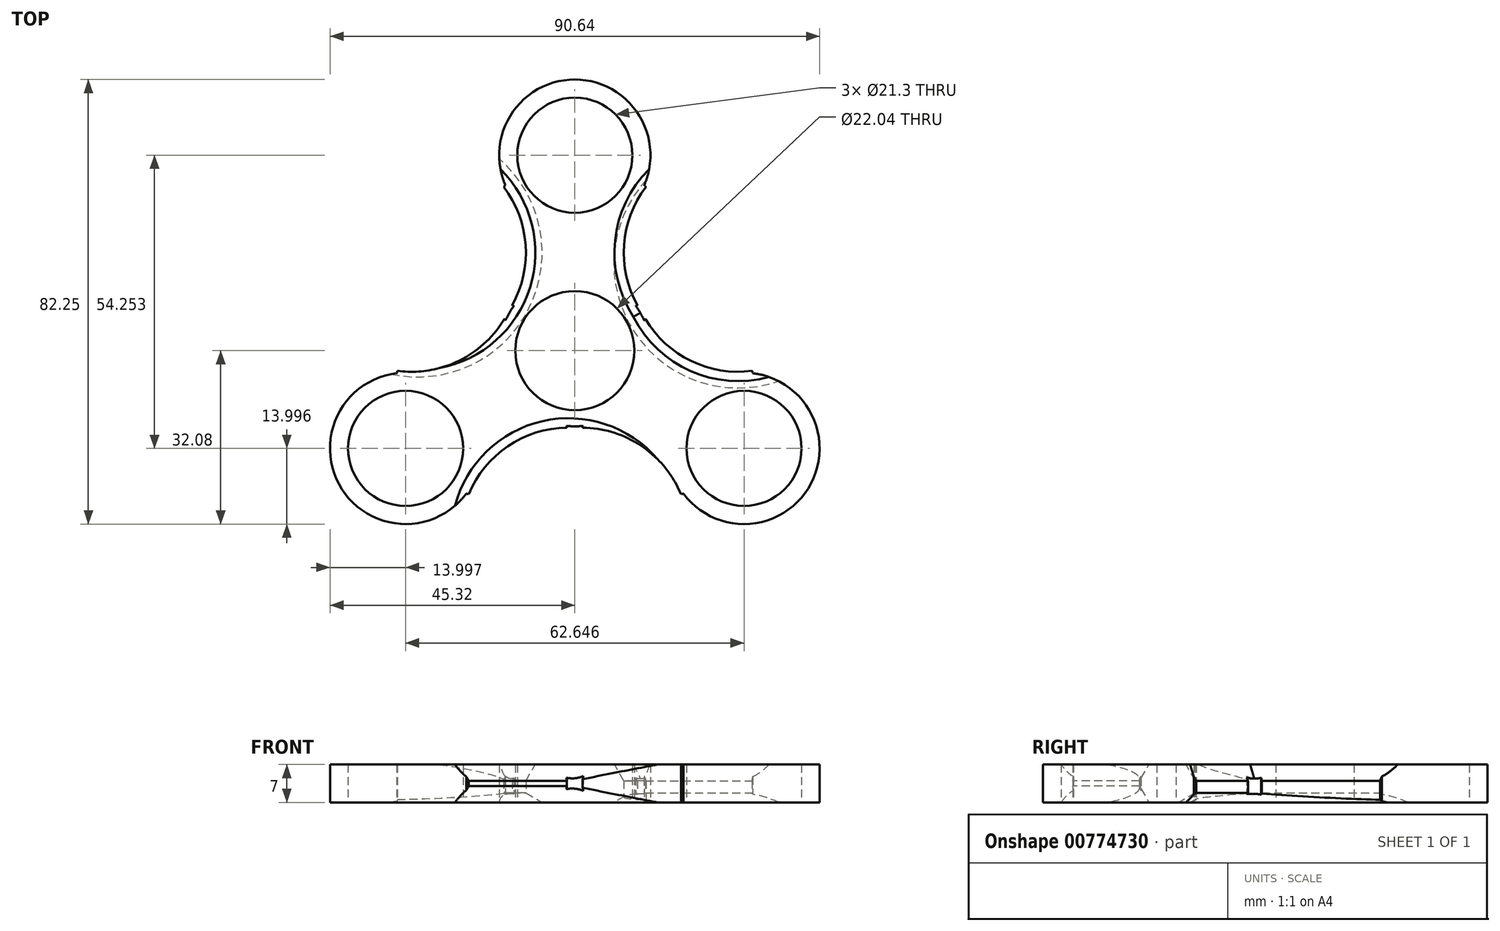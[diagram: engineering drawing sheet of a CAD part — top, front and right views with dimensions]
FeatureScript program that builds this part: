
annotation { "Feature Type Name" : "Feature", "Feature Type Description" : "" }
export const myFeature = defineFeature(function(context is Context, id is Id, definition is map)
    precondition{}
    {
        {
            var Q0;
            Q0=qCreatedBy(makeId("Top.planeOp"),FACE);
            var sketch = newSketch(context, id + "F0", { "sketchPlane" : qUnion([Q0])});
            skCircle(sketch, "E0", {"center": v(0, 0) * mm, "radius": 14 * mm});
            skCircle(sketch, "E1", {"center": v(0, 36.17) * mm, "radius": 14 * mm});
            skPoint(sketch, "E2", {"position": v(0, 18.13) * mm});
            skCircle(sketch, "E3", {"center": v(29.06, 18.13) * mm, "radius": 20 * mm});
            skPoint(sketch, "E4", {"position": v(-29.06, 0) * mm});
            skCircle(sketch, "E5", {"center": v(-29.06, 18.13) * mm, "radius": 20 * mm});
            skCircle(sketch, "E6", {"center": v(0, 18.13) * mm, "radius": 17.93 * mm});
            skCircle(sketch, "E7.1.0", {"center": v(-31.32, -18.08) * mm, "radius": 14 * mm});
            skCircle(sketch, "E7.1.2", {"center": v(-30.23, 16.1) * mm, "radius": 20 * mm});
            skCircle(sketch, "E7.1.3", {"center": v(-1.18, -34.23) * mm, "radius": 20 * mm});
            skCircle(sketch, "E7.1.4", {"center": v(-15.7, -9.07) * mm, "radius": 17.93 * mm});
            skCircle(sketch, "E7.2.0", {"center": v(31.32, -18.08) * mm, "radius": 14 * mm});
            skCircle(sketch, "E7.2.2", {"center": v(1.18, -34.23) * mm, "radius": 20 * mm});
            skCircle(sketch, "E7.2.3", {"center": v(30.23, 16.1) * mm, "radius": 20 * mm});
            skCircle(sketch, "E7.2.4", {"center": v(15.7, -9.07) * mm, "radius": 17.93 * mm});
            skCircle(sketch, "E8", {"center": v(0, 0) * mm, "radius": 11.02 * mm});
            skCircle(sketch, "E9", {"center": v(0, 36.17) * mm, "radius": 10.65 * mm});
            skCircle(sketch, "E10", {"center": v(-31.32, -18.08) * mm, "radius": 10.65 * mm});
            skCircle(sketch, "E11", {"center": v(31.32, -18.08) * mm, "radius": 10.65 * mm});
            skSolve(sketch);
        }
        {
            var Q0;
            {var subQ0=sQuery(id+"F0.wireOp",EDGE,"E7.2.4");var subQ1=sQuery(id+"F0.wireOp",EDGE,"E7.2.0");var subQ2=makeQuery(id+"F0.imprint","INTERSECT",VERTEX,{"disambiguationData":[OD(0.0)],"derivedFrom":[subQ1,subQ0]});Q0=makeQuery(id+"F0.imprint","IMPRINT",FACE,{"disambiguationData":[TD([[makeQuery(id+"F0.imprint","IMPRINT",EDGE,{"disambiguationData":[TD([[subQ2,-1.0]])],"derivedFrom":subQ1}),1.0]])]});}
            var Q1;
            {var subQ0=sQuery(id+"F0.wireOp",EDGE,"E7.2.4");var subQ1=sQuery(id+"F0.wireOp",EDGE,"E7.2.0");var subQ2=makeQuery(id+"F0.imprint","INTERSECT",VERTEX,{"disambiguationData":[OD(0.0)],"derivedFrom":[subQ1,subQ0]});Q1=makeQuery(id+"F0.imprint","IMPRINT",FACE,{"disambiguationData":[TD([[makeQuery(id+"F0.imprint","IMPRINT",EDGE,{"disambiguationData":[TD([[subQ2,1.0]])],"derivedFrom":subQ1}),1.0]])]});}
            var Q2;
            {var subQ5=sQuery(id+"F0.wireOp",EDGE,"E0");var subQ9=sQuery(id+"F0.wireOp",EDGE,"E6");var subQ10=makeQuery(id+"F0.imprint","INTERSECT",VERTEX,{"disambiguationData":[OD(0.0)],"derivedFrom":[subQ5,subQ9]});Q2=makeQuery(id+"F0.imprint","IMPRINT",FACE,{"disambiguationData":[TD([[makeQuery(id+"F0.imprint","IMPRINT",EDGE,{"disambiguationData":[TD([[subQ10,1.0]])],"derivedFrom":subQ5}),-1.0]])]});}
            var Q3;
            {var subQ0=sQuery(id+"F0.wireOp",EDGE,"E6");var subQ1=sQuery(id+"F0.wireOp",EDGE,"B8NFszW9-JFWc-HDjk-8WFd-a5gvqLxuiGRg");var subQ2=makeQuery(id+"F0.imprint","INTERSECT",VERTEX,{"disambiguationData":[OD(0.0)],"derivedFrom":[subQ1,subQ0]});Q3=makeQuery(id+"F0.imprint","IMPRINT",FACE,{"disambiguationData":[TD([[makeQuery(id+"F0.imprint","IMPRINT",EDGE,{"disambiguationData":[TD([[subQ2,1.0]])],"derivedFrom":subQ1}),-1.0]])]});}
            var Q4;
            {var subQ0=sQuery(id+"F0.wireOp",EDGE,"E6");var subQ1=sQuery(id+"F0.wireOp",EDGE,"B8NFszW9-JFWc-HDjk-8WFd-a5gvqLxuiGRg");var subQ2=makeQuery(id+"F0.imprint","INTERSECT",VERTEX,{"disambiguationData":[OD(1.0)],"derivedFrom":[subQ1,subQ0]});Q4=makeQuery(id+"F0.imprint","IMPRINT",FACE,{"disambiguationData":[TD([[makeQuery(id+"F0.imprint","IMPRINT",EDGE,{"disambiguationData":[TD([[subQ2,-1.0]])],"derivedFrom":subQ1}),-1.0]])]});}
            var Q5;
            {var subQ0=sQuery(id+"F0.wireOp",EDGE,"E7.2.4");var subQ1=sQuery(id+"F0.wireOp",EDGE,"B8NFszW9-JFWc-HDjk-8WFd-a5gvqLxuiGRg");var subQ2=makeQuery(id+"F0.imprint","INTERSECT",VERTEX,{"disambiguationData":[OD(1.0)],"derivedFrom":[subQ1,subQ0]});Q5=makeQuery(id+"F0.imprint","IMPRINT",FACE,{"disambiguationData":[TD([[makeQuery(id+"F0.imprint","IMPRINT",EDGE,{"disambiguationData":[TD([[subQ2,-1.0]])],"derivedFrom":subQ1}),-1.0]])]});}
            var Q6;
            {var subQ0=sQuery(id+"F0.wireOp",EDGE,"E7.2.4");var subQ1=sQuery(id+"F0.wireOp",EDGE,"B8NFszW9-JFWc-HDjk-8WFd-a5gvqLxuiGRg");var subQ2=makeQuery(id+"F0.imprint","INTERSECT",VERTEX,{"disambiguationData":[OD(0.0)],"derivedFrom":[subQ1,subQ0]});Q6=makeQuery(id+"F0.imprint","IMPRINT",FACE,{"disambiguationData":[TD([[makeQuery(id+"F0.imprint","IMPRINT",EDGE,{"disambiguationData":[TD([[subQ2,-1.0]])],"derivedFrom":subQ1}),-1.0]])]});}
            var Q7;
            {var subQ0=sQuery(id+"F0.wireOp",EDGE,"E7.1.4");var subQ1=sQuery(id+"F0.wireOp",EDGE,"B8NFszW9-JFWc-HDjk-8WFd-a5gvqLxuiGRg");var subQ2=makeQuery(id+"F0.imprint","INTERSECT",VERTEX,{"disambiguationData":[OD(0.0)],"derivedFrom":[subQ1,subQ0]});Q7=makeQuery(id+"F0.imprint","IMPRINT",FACE,{"disambiguationData":[TD([[makeQuery(id+"F0.imprint","IMPRINT",EDGE,{"disambiguationData":[TD([[subQ2,-1.0]])],"derivedFrom":subQ1}),-1.0]])]});}
            var Q8;
            {var subQ0=sQuery(id+"F0.wireOp",EDGE,"E7.2.4");var subQ1=sQuery(id+"F0.wireOp",EDGE,"B8NFszW9-JFWc-HDjk-8WFd-a5gvqLxuiGRg");var subQ2=makeQuery(id+"F0.imprint","INTERSECT",VERTEX,{"disambiguationData":[OD(0.0)],"derivedFrom":[subQ1,subQ0]});Q8=makeQuery(id+"F0.imprint","IMPRINT",FACE,{"disambiguationData":[TD([[makeQuery(id+"F0.imprint","IMPRINT",EDGE,{"disambiguationData":[TD([[subQ2,1.0]])],"derivedFrom":subQ1}),-1.0]])]});}
            var Q9;
            {var subQ3=sQuery(id+"F0.wireOp",EDGE,"E6");var subQ8=sQuery(id+"F0.wireOp",EDGE,"E0");var subQ9=makeQuery(id+"F0.imprint","INTERSECT",VERTEX,{"disambiguationData":[OD(1.0)],"derivedFrom":[subQ8,subQ3]});Q9=makeQuery(id+"F0.imprint","IMPRINT",FACE,{"disambiguationData":[TD([[makeQuery(id+"F0.imprint","IMPRINT",EDGE,{"disambiguationData":[TD([[subQ9,-1.0]])],"derivedFrom":subQ8}),-1.0]])]});}
            var Q10;
            {var subQ0=sQuery(id+"F0.wireOp",EDGE,"E7.1.4");var subQ1=sQuery(id+"F0.wireOp",EDGE,"E7.1.0");var subQ2=makeQuery(id+"F0.imprint","INTERSECT",VERTEX,{"disambiguationData":[OD(0.0)],"derivedFrom":[subQ1,subQ0]});Q10=makeQuery(id+"F0.imprint","IMPRINT",FACE,{"disambiguationData":[TD([[makeQuery(id+"F0.imprint","IMPRINT",EDGE,{"disambiguationData":[TD([[subQ2,1.0]])],"derivedFrom":subQ1}),1.0]])]});}
            var Q11;
            {var subQ0=sQuery(id+"F0.wireOp",EDGE,"E7.1.4");var subQ1=sQuery(id+"F0.wireOp",EDGE,"E7.1.0");var subQ2=makeQuery(id+"F0.imprint","INTERSECT",VERTEX,{"disambiguationData":[OD(0.0)],"derivedFrom":[subQ1,subQ0]});Q11=makeQuery(id+"F0.imprint","IMPRINT",FACE,{"disambiguationData":[TD([[makeQuery(id+"F0.imprint","IMPRINT",EDGE,{"disambiguationData":[TD([[subQ2,-1.0]])],"derivedFrom":subQ1}),1.0]])]});}
            var Q12;
            {var subQ0=sQuery(id+"F0.wireOp",EDGE,"E6");var subQ1=sQuery(id+"F0.wireOp",EDGE,"SfOP9qtQ-fiCl-8aQM-pGTJ-PSkb9JabpYto");var subQ2=makeQuery(id+"F0.imprint","INTERSECT",VERTEX,{"disambiguationData":[OD(0.0)],"derivedFrom":[subQ1,subQ0]});Q12=makeQuery(id+"F0.imprint","IMPRINT",FACE,{"disambiguationData":[TD([[makeQuery(id+"F0.imprint","IMPRINT",EDGE,{"disambiguationData":[TD([[subQ2,1.0]])],"derivedFrom":subQ1}),-1.0]])]});}
            var Q13;
            {var subQ0=sQuery(id+"F0.wireOp",EDGE,"E6");var subQ1=sQuery(id+"F0.wireOp",EDGE,"SfOP9qtQ-fiCl-8aQM-pGTJ-PSkb9JabpYto");var subQ2=makeQuery(id+"F0.imprint","INTERSECT",VERTEX,{"disambiguationData":[OD(0.0)],"derivedFrom":[subQ1,subQ0]});Q13=makeQuery(id+"F0.imprint","IMPRINT",FACE,{"disambiguationData":[TD([[makeQuery(id+"F0.imprint","IMPRINT",EDGE,{"disambiguationData":[TD([[subQ2,-1.0]])],"derivedFrom":subQ1}),-1.0]])]});}
            var Q14;
            {var subQ7=sQuery(id+"F0.wireOp",EDGE,"E7.2.4");var subQ12=sQuery(id+"F0.wireOp",EDGE,"E0");var subQ14=makeQuery(id+"F0.imprint","INTERSECT",VERTEX,{"disambiguationData":[OD(0.0)],"derivedFrom":[subQ12,subQ7]});Q14=makeQuery(id+"F0.imprint","IMPRINT",FACE,{"disambiguationData":[TD([[makeQuery(id+"F0.imprint","IMPRINT",EDGE,{"disambiguationData":[TD([[subQ14,-1.0]])],"derivedFrom":subQ12}),-1.0]])]});}
            var Q15;
            {var subQ0=sQuery(id+"F0.wireOp",EDGE,"E6");var subQ1=sQuery(id+"F0.wireOp",EDGE,"E1");var subQ2=makeQuery(id+"F0.imprint","INTERSECT",VERTEX,{"disambiguationData":[OD(0.0)],"derivedFrom":[subQ1,subQ0]});Q15=makeQuery(id+"F0.imprint","IMPRINT",FACE,{"disambiguationData":[TD([[makeQuery(id+"F0.imprint","IMPRINT",EDGE,{"disambiguationData":[TD([[subQ2,1.0]])],"derivedFrom":subQ1}),1.0]])]});}
            var Q16;
            {var subQ0=sQuery(id+"F0.wireOp",EDGE,"E6");var subQ1=sQuery(id+"F0.wireOp",EDGE,"E1");var subQ2=makeQuery(id+"F0.imprint","INTERSECT",VERTEX,{"disambiguationData":[OD(0.0)],"derivedFrom":[subQ1,subQ0]});Q16=makeQuery(id+"F0.imprint","IMPRINT",FACE,{"disambiguationData":[TD([[makeQuery(id+"F0.imprint","IMPRINT",EDGE,{"disambiguationData":[TD([[subQ2,-1.0]])],"derivedFrom":subQ1}),1.0]])]});}
            var Q17;
            {var subQ0=sQuery(id+"F0.wireOp",EDGE,"E6");var subQ1=sQuery(id+"F0.wireOp",EDGE,"E0");var subQ2=makeQuery(id+"F0.imprint","INTERSECT",VERTEX,{"disambiguationData":[OD(0.0)],"derivedFrom":[subQ1,subQ0]});Q17=makeQuery(id+"F0.imprint","IMPRINT",FACE,{"disambiguationData":[TD([[makeQuery(id+"F0.imprint","IMPRINT",EDGE,{"disambiguationData":[TD([[subQ2,1.0]])],"derivedFrom":subQ1}),1.0]])]});}
            var Q18;
            {var subQ0=sQuery(id+"F0.wireOp",EDGE,"E6");var subQ1=sQuery(id+"F0.wireOp",EDGE,"E0");var subQ2=makeQuery(id+"F0.imprint","INTERSECT",VERTEX,{"disambiguationData":[OD(1.0)],"derivedFrom":[subQ1,subQ0]});Q18=makeQuery(id+"F0.imprint","IMPRINT",FACE,{"disambiguationData":[TD([[makeQuery(id+"F0.imprint","IMPRINT",EDGE,{"disambiguationData":[TD([[subQ2,-1.0]])],"derivedFrom":subQ1}),1.0]])]});}
            var Q19;
            {var subQ0=sQuery(id+"F0.wireOp",EDGE,"E7.2.4");var subQ1=sQuery(id+"F0.wireOp",EDGE,"E0");var subQ2=makeQuery(id+"F0.imprint","INTERSECT",VERTEX,{"disambiguationData":[OD(1.0)],"derivedFrom":[subQ1,subQ0]});Q19=makeQuery(id+"F0.imprint","IMPRINT",FACE,{"disambiguationData":[TD([[makeQuery(id+"F0.imprint","IMPRINT",EDGE,{"disambiguationData":[TD([[subQ2,-1.0]])],"derivedFrom":subQ1}),1.0]])]});}
            var Q20;
            {var subQ0=sQuery(id+"F0.wireOp",EDGE,"E7.2.4");var subQ1=sQuery(id+"F0.wireOp",EDGE,"E0");var subQ2=makeQuery(id+"F0.imprint","INTERSECT",VERTEX,{"disambiguationData":[OD(0.0)],"derivedFrom":[subQ1,subQ0]});Q20=makeQuery(id+"F0.imprint","IMPRINT",FACE,{"disambiguationData":[TD([[makeQuery(id+"F0.imprint","IMPRINT",EDGE,{"disambiguationData":[TD([[subQ2,1.0]])],"derivedFrom":subQ1}),1.0]])]});}
            var Q21;
            {var subQ0=sQuery(id+"F0.wireOp",EDGE,"E7.2.4");var subQ1=sQuery(id+"F0.wireOp",EDGE,"E0");var subQ2=makeQuery(id+"F0.imprint","INTERSECT",VERTEX,{"disambiguationData":[OD(0.0)],"derivedFrom":[subQ1,subQ0]});Q21=makeQuery(id+"F0.imprint","IMPRINT",FACE,{"disambiguationData":[TD([[makeQuery(id+"F0.imprint","IMPRINT",EDGE,{"disambiguationData":[TD([[subQ2,-1.0]])],"derivedFrom":subQ1}),1.0]])]});}
            var Q22;
            {var subQ0=sQuery(id+"F0.wireOp",EDGE,"E7.1.4");var subQ1=sQuery(id+"F0.wireOp",EDGE,"E0");var subQ2=makeQuery(id+"F0.imprint","INTERSECT",VERTEX,{"disambiguationData":[OD(0.0)],"derivedFrom":[subQ1,subQ0]});Q22=makeQuery(id+"F0.imprint","IMPRINT",FACE,{"disambiguationData":[TD([[makeQuery(id+"F0.imprint","IMPRINT",EDGE,{"disambiguationData":[TD([[subQ2,-1.0]])],"derivedFrom":subQ1}),1.0]])]});}
            extrude(context, id + "F1", {"entities" : qUnion([Q0, Q1, Q2, Q3, Q4, Q5, Q6, Q7, Q8, Q9, Q10, Q11, Q12, Q13, Q14, Q15, Q16, Q17, Q18, Q19, Q20, Q21, Q22]), "depth" : 7 * mm, "offsetDistance" : 25 * mm});
        }
        {
            var Q0;
            Q0=makeQuery(id+"F1.opExtrude","CAP_EDGE",EDGE,{"disambiguationData":[OSD([sQuery(id+"F0.wireOp",EDGE,"E7.1.3")])],"isStart":false});
            var Q1;
            Q1=makeQuery(id+"F1.opExtrude","CAP_EDGE",EDGE,{"disambiguationData":[OSD([sQuery(id+"F0.wireOp",EDGE,"E3")])],"isStart":false});
            var Q2;
            Q2=makeQuery(id+"F1.opExtrude","CAP_EDGE",EDGE,{"disambiguationData":[OSD([sQuery(id+"F0.wireOp",EDGE,"E7.1.3")])],"isStart":true});
            var Q3;
            Q3=makeQuery(id+"F1.opExtrude","CAP_EDGE",EDGE,{"disambiguationData":[OSD([sQuery(id+"F0.wireOp",EDGE,"E7.2.3")])],"isStart":false});
            var Q4;
            Q4=makeQuery(id+"F1.opExtrude","CAP_EDGE",EDGE,{"disambiguationData":[OSD([sQuery(id+"F0.wireOp",EDGE,"E5")])],"isStart":true});
            var Q5;
            Q5=makeQuery(id+"F1.opExtrude","CAP_EDGE",EDGE,{"disambiguationData":[OSD([sQuery(id+"F0.wireOp",EDGE,"E5")])],"isStart":false});
            var Q6;
            Q6=makeQuery(id+"F1.opExtrude","CAP_EDGE",EDGE,{"disambiguationData":[OSD([sQuery(id+"F0.wireOp",EDGE,"E7.2.3")])],"isStart":true});
            chamfer(context, id + "F2", {"entities" : qUnion([Q0, Q1, Q2, Q3, Q4, Q5, Q6]), "chamferType" : ChamferType.OFFSET_ANGLE, "width" : 3 * mm, "oppositeDirection" : false, "angle" : 30 * degree, "tangentPropagation" : true});
        }
    });
